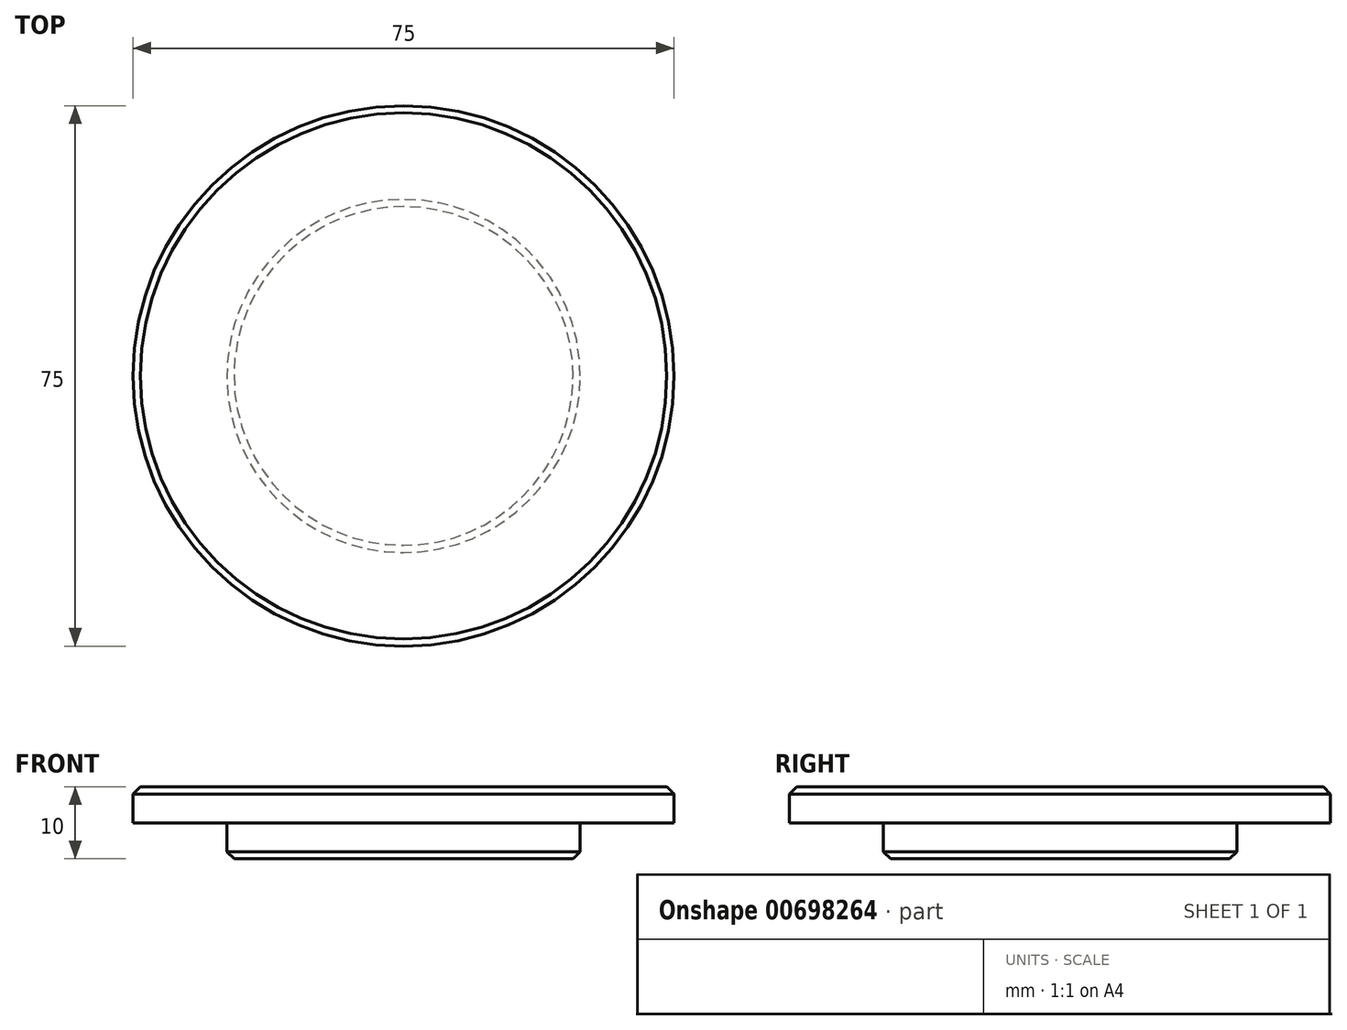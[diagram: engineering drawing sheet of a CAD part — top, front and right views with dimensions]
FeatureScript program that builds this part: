
annotation { "Feature Type Name" : "Feature", "Feature Type Description" : "" }
export const myFeature = defineFeature(function(context is Context, id is Id, definition is map)
    precondition{}
    {
        {
            var Q0;
            Q0=qCreatedBy(makeId("Top.planeOp"),FACE);
            var sketch = newSketch(context, id + "F0", { "sketchPlane" : qUnion([Q0])});
            skCircle(sketch, "E0", {"center": v(0, 0) * mm, "radius": 24.5 * mm});
            skSolve(sketch);
        }
        {
            var Q0;
            Q0=makeQuery(id+"F0.imprint","IMPRINT",FACE,{"disambiguationData":[TD([[makeQuery(id+"F0.imprint","IMPRINT",EDGE,{"derivedFrom":sQuery(id+"F0.wireOp",EDGE,"E0")}),1.0]])]});
            extrude(context, id + "F1", {"entities" : qUnion([Q0]), "depth" : 5 * mm, "offsetDistance" : 25 * mm});
        }
        {
            var Q0;
            Q0=makeQuery(id+"F1.opExtrude","CAP_FACE",FACE,{"disambiguationData":[OSD([sQuery(id+"F0.wireOp",EDGE,"E0")])],"isStart":false});
            var sketch = newSketch(context, id + "F2", { "sketchPlane" : qUnion([Q0])});
            skCircle(sketch, "E1", {"center": v(0, 0) * mm, "radius": 37.5 * mm});
            skSolve(sketch);
        }
        {
            var Q0;
            Q0=makeQuery(id+"F2.imprint","IMPRINT",FACE,{"disambiguationData":[TD([[makeQuery(id+"F2.imprint","IMPRINT",EDGE,{"derivedFrom":sQuery(id+"F2.wireOp",EDGE,"E1")}),1.0]])]});
            var Q1;
            Q1=makeQuery(id+"F2.imprint","IMPRINT",FACE,{"disambiguationData":[TD([[makeQuery(id+"F2.imprint","IMPRINT",EDGE,{"derivedFrom":makeQuery(id+"F1.opExtrude","CAP_EDGE",EDGE,{"disambiguationData":[OSD([sQuery(id+"F0.wireOp",EDGE,"E0")])],"isStart":false})}),1.0]])]});
            extrude(context, id + "F3", {"entities" : qUnion([Q0, Q1]), "operationType" : NewBodyOperationType.ADD, "depth" : 5 * mm, "offsetDistance" : 25 * mm});
        }
        {
            var Q0;
            Q0=makeQuery(id+"F3.opExtrude","CAP_EDGE",EDGE,{"disambiguationData":[OSD([sQuery(id+"F2.wireOp",EDGE,"E1")])],"isStart":false});
            chamfer(context, id + "F4", {"entities" : qUnion([Q0]), "width" : 1 * mm, "tangentPropagation" : true});
        }
        {
            var Q0;
            Q0=makeQuery(id+"F1.opExtrude","CAP_EDGE",EDGE,{"disambiguationData":[OSD([sQuery(id+"F0.wireOp",EDGE,"E0")])],"isStart":true});
            chamfer(context, id + "F5", {"entities" : qUnion([Q0]), "width" : 1 * mm, "tangentPropagation" : true});
        }
    });
